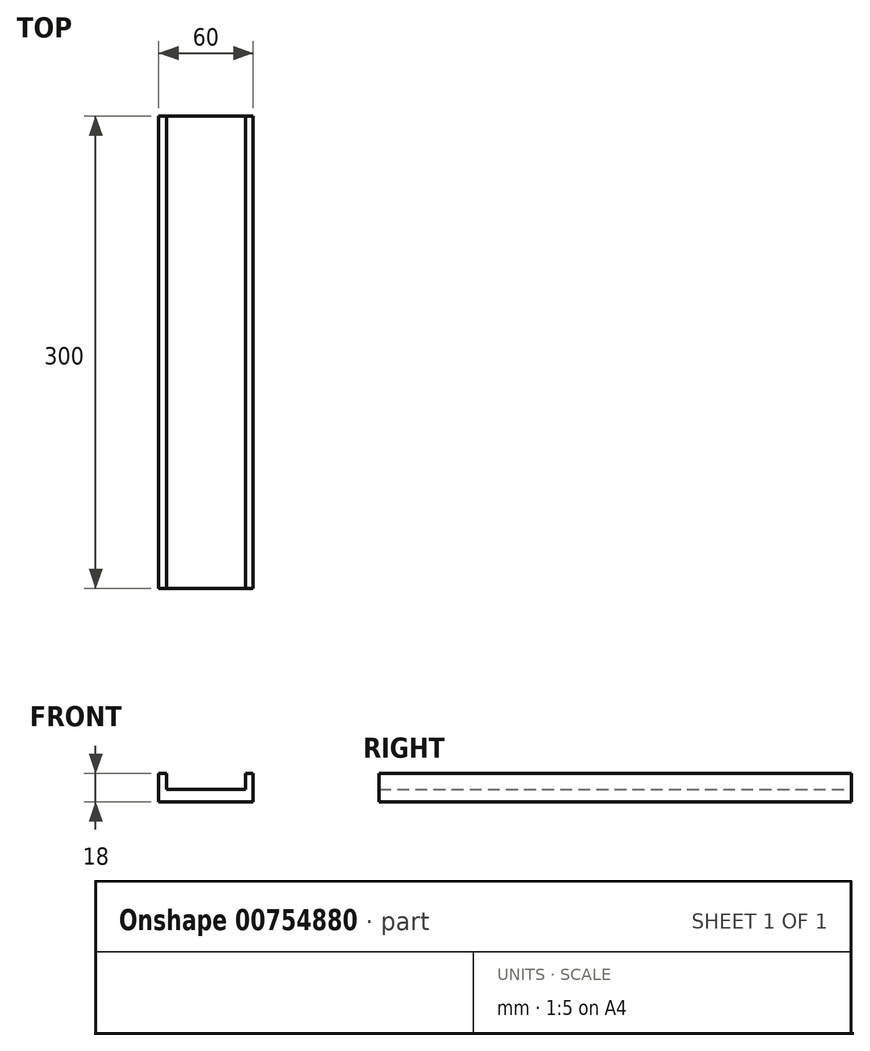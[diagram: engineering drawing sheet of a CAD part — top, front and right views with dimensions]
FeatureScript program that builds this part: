
annotation { "Feature Type Name" : "Feature", "Feature Type Description" : "" }
export const myFeature = defineFeature(function(context is Context, id is Id, definition is map)
    precondition{}
    {
        {
            var Q0;
            Q0=qCreatedBy(makeId("Front.planeOp"),FACE);
            var sketch = newSketch(context, id + "F0", { "sketchPlane" : qUnion([Q0])});
            skLineSegment(sketch, "E0", {"start": v(-35.6, 0) * mm, "end": v(48.4, 0) * mm, "construction": true});
            skLineSegment(sketch, "E1.bottom", {"start": v(-23.22, 18) * mm, "end": v(-18.22, 18) * mm});
            skLineSegment(sketch, "E1.top", {"start": v(-23.22, 0) * mm, "end": v(36.78, 0) * mm});
            skLineSegment(sketch, "E1.left", {"start": v(-23.22, 18) * mm, "end": v(-23.22, 0) * mm});
            skLineSegment(sketch, "E1.right", {"start": v(36.78, 18) * mm, "end": v(36.78, 0) * mm});
            skLineSegment(sketch, "E2.top", {"start": v(-18.22, 8) * mm, "end": v(31.78, 8) * mm});
            skLineSegment(sketch, "E2.left", {"start": v(-18.22, 18) * mm, "end": v(-18.22, 8) * mm});
            skLineSegment(sketch, "E2.right", {"start": v(31.78, 18) * mm, "end": v(31.78, 8) * mm});
            skLineSegment(sketch, "E3.trimOffspring", {"start": v(31.78, 18) * mm, "end": v(36.78, 18) * mm});
            skSolve(sketch);
        }
        {
            var Q0;
            Q0 = qSketchRegion(id + "F0", true);
            extrude(context, id + "F1", {"entities" : qUnion([Q0]), "depth" : 50 * 6 * mm, "offsetDistance" : 25 * mm});
        }
    });
